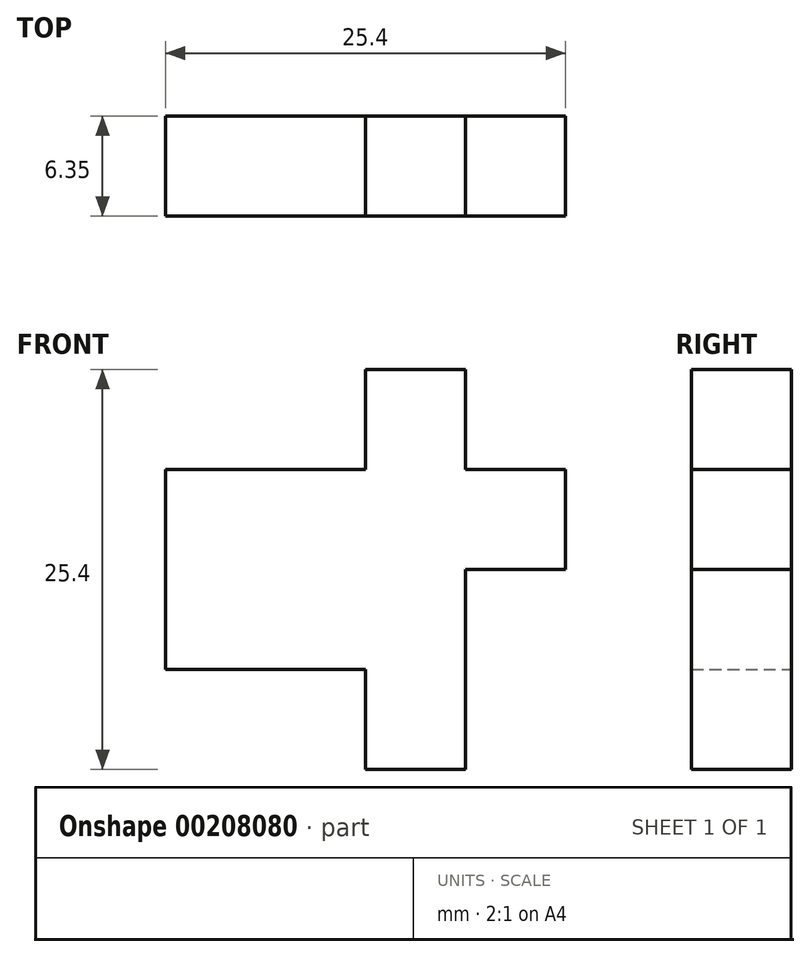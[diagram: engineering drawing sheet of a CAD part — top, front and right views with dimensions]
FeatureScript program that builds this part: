
annotation { "Feature Type Name" : "Feature", "Feature Type Description" : "" }
export const myFeature = defineFeature(function(context is Context, id is Id, definition is map)
    precondition{}
    {
        {
            var Q0;
            Q0=qCreatedBy(makeId("Front.planeOp"),FACE);
            var sketch = newSketch(context, id + "F0", { "sketchPlane" : qUnion([Q0])});
            skLineSegment(sketch, "E0", {"start": v(0, 0) * mm, "end": v(0, 19.06) * mm});
            skLineSegment(sketch, "E1", {"start": v(0, 0) * mm, "end": v(0, 19.05) * mm});
            skLineSegment(sketch, "E2", {"start": v(0, 19.06) * mm, "end": v(12.7, 19.06) * mm});
            skLineSegment(sketch, "E3", {"start": v(12.7, 19.06) * mm, "end": v(12.7, 25.4) * mm});
            skLineSegment(sketch, "E4", {"start": v(12.7, 25.4) * mm, "end": v(19.05, 25.4) * mm});
            skLineSegment(sketch, "E5", {"start": v(19.05, 25.4) * mm, "end": v(19.05, 19.05) * mm});
            skLineSegment(sketch, "E6", {"start": v(19.05, 19.05) * mm, "end": v(25.4, 19.05) * mm});
            skLineSegment(sketch, "E7", {"start": v(25.4, 19.05) * mm, "end": v(25.4, 12.7) * mm});
            skLineSegment(sketch, "E8", {"start": v(19.05, 0) * mm, "end": v(19.05, 12.7) * mm});
            skLineSegment(sketch, "E9", {"start": v(25.4, 12.7) * mm, "end": v(19.05, 12.7) * mm});
            skLineSegment(sketch, "E10", {"start": v(12.7, 0) * mm, "end": v(19.05, 0) * mm});
            skLineSegment(sketch, "E11", {"start": v(12.7, 0) * mm, "end": v(12.7, 6.35) * mm});
            skLineSegment(sketch, "E12", {"start": v(12.7, 6.35) * mm, "end": v(0, 6.35) * mm});
            skSolve(sketch);
        }
        {
            var Q0;
            {var subQ0=sQuery(id+"F0.wireOp",EDGE,"E0");Q0=makeQuery(id+"F0.imprint","IMPRINT",FACE,{"disambiguationData":[TD([[makeQuery(id+"F0.imprint","IMPRINT",EDGE,{"derivedFrom":subQ0}),-1.0]])]});}
            extrude(context, id + "F1", {"entities" : qUnion([Q0]), "depth" : 6.35 * mm});
        }
    });
